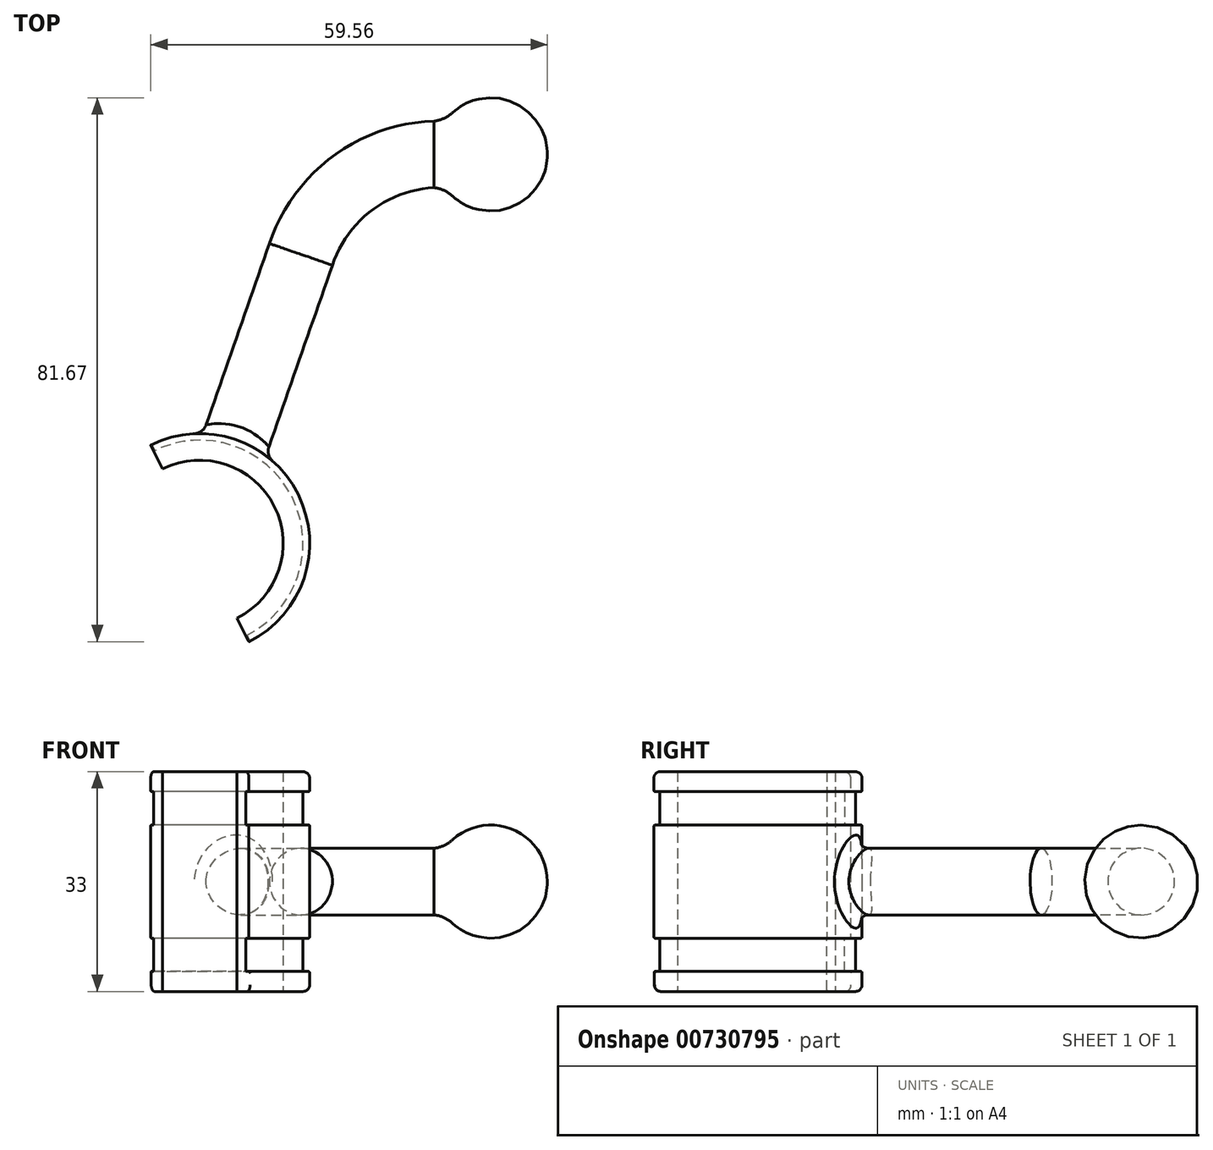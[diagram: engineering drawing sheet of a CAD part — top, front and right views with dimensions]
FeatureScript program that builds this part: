
annotation { "Feature Type Name" : "Feature", "Feature Type Description" : "" }
export const myFeature = defineFeature(function(context is Context, id is Id, definition is map)
    precondition{}
    {
        {
            var Q0;
            Q0=qCreatedBy(makeId("Top.planeOp"),FACE);
            var sketch = newSketch(context, id + "F0", { "sketchPlane" : qUnion([Q0])});
            skLineSegment(sketch, "E0", {"start": v(-8.5, 0) * mm, "end": v(-11.82, 0) * mm});
            skArc(sketch, "E1", {"start": v(8.5, 0) * mm, "mid": v(2.63, 8.08) * mm, "end": v(-6.87, 5) * mm});
            skLineSegment(sketch, "E2", {"start": v(50.87, 0) * mm, "end": v(0, 0) * mm, "construction": true});
            skLineSegment(sketch, "E3", {"start": v(8.5, 0) * mm, "end": v(0, 0) * mm});
            skLineSegment(sketch, "E4", {"start": v(-11.82, 0) * mm, "end": v(-5.91, 0) * mm});
            skLineSegment(sketch, "E5", {"start": v(-5.91, 0) * mm, "end": v(0, 0) * mm});
            skPoint(sketch, "E6", {"position": v(-28.5, -15) * mm});
            skLineSegment(sketch, "E7", {"start": v(0, 0) * mm, "end": v(-93.44, 0) * mm, "construction": true});
            skLineSegment(sketch, "E8", {"start": v(-8.5, 5) * mm, "end": v(-6.87, 5) * mm});
            skLineSegment(sketch, "E9", {"start": v(-52.11, -35.8) * mm, "end": v(-46.57, -38.1) * mm});
            skLineSegment(sketch, "E10", {"start": v(-8.5, 5) * mm, "end": v(-8.5, 0) * mm});
            skSolve(sketch);
        }
        {
            var Q0;
            Q0=makeQuery(id+"F0.imprint","IMPRINT",FACE,{"disambiguationData":[TD([[makeQuery(id+"F0.imprint","IMPRINT",EDGE,{"derivedFrom":sQuery(id+"F0.wireOp",EDGE,"E1")}),1.0]])]});
            var Q1;
            Q1=sQuery(id+"F0.wireOp",EDGE,"E3");
            revolve(context, id + "F1", {"surfaceOperationType" : NewSurfaceOperationType.NEW, "entities" : qUnion([Q0]), "axis" : qUnion([Q1]), "revolveType" : RevolveType.FULL});
        }
        {
            var Q0;
            Q0=makeQuery(id+"F1.opRevolve","SWEPT_FACE",FACE,{"disambiguationData":[OSD([sQuery(id+"F0.wireOp",EDGE,"E10")])]});
            var sketch = newSketch(context, id + "F2", { "sketchPlane" : qUnion([Q0])});
            skCircle(sketch, "E11.0", {"center": v(0, 0) * mm, "radius": 5 * mm});
            skSolve(sketch);
        }
        {
            var Q0;
            Q0=makeQuery(id+"F1.opRevolve","SWEPT_EDGE",EDGE,{"disambiguationData":[OSD([sQuery(id+"F0.wireOp",EDGE,"E1"),sQuery(id+"F0.wireOp",EDGE,"E8")])]});
            fillet(context, id + "F3", {"entities" : qUnion([Q0]), "radius" : 5 * mm, "tangentPropagation" : true, "allowEdgeOverflow" : false});
        }
        {
            var Q0;
            Q0=qCreatedBy(makeId("Top.planeOp"),FACE);
            var sketch = newSketch(context, id + "F4", { "sketchPlane" : qUnion([Q0])});
            skLineSegment(sketch, "E12.0", {"start": v(-33.35, -45.22) * mm, "end": v(-34.25, -44.88) * mm});
            skPoint(sketch, "E13.first.point", {"position": v(-38.02, -43.45) * mm});
            skPoint(sketch, "E13.second.point", {"position": v(-44.06, -59.28) * mm});
            skPoint(sketch, "E13.third.point", {"position": v(-42.18, -43.45) * mm});
            skPoint(sketch, "E13.third.point.positionSnap0", {"position": v(-38.02, -43.45) * mm});
            skPoint(sketch, "E14", {"position": v(-40.1, -51.73) * mm});
            skLineSegment(sketch, "E15", {"start": v(-38.02, -43.45) * mm, "end": v(-43.7, -58.41) * mm});
            skArc(sketch, "E16", {"start": v(-38.1, -69.6) * mm, "mid": v(-32.5, -52.83) * mm, "end": v(-49.27, -47.23) * mm});
            skLineSegment(sketch, "E17.0", {"start": v(-38.02, -43.45) * mm, "end": v(-38.02, -43.45) * mm});
            skArc(sketch, "E18.0", {"start": v(-36.32, -73.17) * mm, "mid": v(-28.93, -51.04) * mm, "end": v(-51.06, -43.65) * mm});
            skLineSegment(sketch, "E19", {"start": v(-51.06, -43.65) * mm, "end": v(-49.27, -47.23) * mm});
            skLineSegment(sketch, "E20", {"start": v(-38.1, -69.6) * mm, "end": v(-36.32, -73.17) * mm});
            skPoint(sketch, "E21.orphan", {"position": v(-42.7, -41.68) * mm});
            skPoint(sketch, "E22.trimOffspring.end.orphan", {"position": v(-41.8, -42.02) * mm});
            skSolve(sketch);
        }
        {
            var Q0;
            {var subQ0=sQuery(id+"F4.wireOp",EDGE,"E19");Q0=makeQuery(id+"F4.imprint","IMPRINT",FACE,{"disambiguationData":[TD([[makeQuery(id+"F4.imprint","IMPRINT",EDGE,{"derivedFrom":subQ0}),1.0]])]});}
            var Q1;
            {var subQ4=sQuery(id+"F4.wireOp",EDGE,"E13");Q1=makeQuery(id+"F4.imprint","IMPRINT",FACE,{"disambiguationData":[TD([[makeQuery(id+"F4.imprint","IMPRINT",EDGE,{"derivedFrom":subQ4}),1.0]])]});}
            extrude(context, id + "F5", {"entities" : qUnion([Q0, Q1]), "operationType" : NewBodyOperationType.ADD, "endBound" : BoundingType.SYMMETRIC, "depth" : 17 * mm, "offsetDistance" : 25 * mm});
        }
        {
            var Q0;
            Q0=makeQuery(id+"F5.opExtrude","CAP_FACE",FACE,{"disambiguationData":[OSD([sQuery(id+"F4.wireOp",EDGE,"E12.0"),sQuery(id+"F4.wireOp",EDGE,"E13"),sQuery(id+"F4.wireOp",EDGE,"E22.trimOffspring"),sQuery(id+"F4.wireOp",EDGE,"E16"),sQuery(id+"F4.wireOp",EDGE,"E18.0"),sQuery(id+"F4.wireOp",EDGE,"E19"),sQuery(id+"F4.wireOp",EDGE,"E20")])],"isStart":false});
            var sketch = newSketch(context, id + "F6", { "sketchPlane" : qUnion([Q0])});
            skArc(sketch, "E23.0", {"start": v(-38.1, -69.6) * mm, "mid": v(-32.5, -52.83) * mm, "end": v(-49.27, -47.23) * mm});
            skArc(sketch, "E24.0", {"start": v(-36.77, -72.28) * mm, "mid": v(-29.82, -51.49) * mm, "end": v(-50.61, -44.54) * mm});
            skLineSegment(sketch, "E25", {"start": v(-49.27, -47.23) * mm, "end": v(-50.61, -44.54) * mm});
            skLineSegment(sketch, "E26", {"start": v(-36.77, -72.28) * mm, "end": v(-38.1, -69.6) * mm});
            skSolve(sketch);
        }
        {
            var Q0;
            Q0=makeQuery(id+"F6.imprint","IMPRINT",FACE,{"disambiguationData":[TD([[makeQuery(id+"F6.imprint","IMPRINT",EDGE,{"derivedFrom":sQuery(id+"F6.wireOp",EDGE,"E23.0")}),-1.0]])]});
            extrude(context, id + "F7", {"entities" : qUnion([Q0]), "depth" : 5 * mm, "offsetDistance" : 25 * mm});
        }
        {
            var Q0;
            Q0=makeQuery(id+"F7.opExtrude","CAP_FACE",FACE,{"disambiguationData":[OSD([sQuery(id+"F6.wireOp",EDGE,"E23.0"),sQuery(id+"F6.wireOp",EDGE,"E24.0"),sQuery(id+"F6.wireOp",EDGE,"E25"),sQuery(id+"F6.wireOp",EDGE,"E26")])],"isStart":false});
            var sketch = newSketch(context, id + "F8", { "sketchPlane" : qUnion([Q0])});
            skArc(sketch, "E27.0", {"start": v(-36.32, -73.17) * mm, "mid": v(-28.93, -51.04) * mm, "end": v(-51.06, -43.65) * mm});
            skLineSegment(sketch, "E28.0", {"start": v(-36.32, -73.17) * mm, "end": v(-36.32, -73.17) * mm});
            skArc(sketch, "E29.0", {"start": v(-38.1, -69.6) * mm, "mid": v(-32.5, -52.83) * mm, "end": v(-49.27, -47.23) * mm});
            skLineSegment(sketch, "E30", {"start": v(-51.06, -43.65) * mm, "end": v(-49.27, -47.23) * mm});
            skLineSegment(sketch, "E31", {"start": v(-36.32, -73.17) * mm, "end": v(-38.1, -69.6) * mm});
            skSolve(sketch);
        }
        {
            var Q0;
            {var subQ0=sQuery(id+"F8.wireOp",EDGE,"E29.0");Q0=makeQuery(id+"F8.imprint","IMPRINT",FACE,{"disambiguationData":[TD([[makeQuery(id+"F8.imprint","IMPRINT",EDGE,{"derivedFrom":subQ0}),-1.0]])]});}
            var Q1;
            {var subQ5=makeQuery(id+"F7.opExtrude","CAP_EDGE",EDGE,{"disambiguationData":[OSD([sQuery(id+"F6.wireOp",EDGE,"E24.0")])],"isStart":false});Q1=makeQuery(id+"F8.imprint","IMPRINT",FACE,{"disambiguationData":[TD([[makeQuery(id+"F8.imprint","IMPRINT",EDGE,{"derivedFrom":subQ5}),-1.0]])]});}
            extrude(context, id + "F9", {"entities" : qUnion([Q0, Q1]), "operationType" : NewBodyOperationType.ADD, "depth" : 3 * mm, "offsetDistance" : 25 * mm});
        }
        {
            var Q0;
            Q0=makeQuery(id+"F7.opExtrude","SWEPT_BODY",BODY,{"disambiguationData":[OSD([sQuery(id+"F6.wireOp",EDGE,"E23.0"),sQuery(id+"F6.wireOp",EDGE,"E24.0"),sQuery(id+"F6.wireOp",EDGE,"E25"),sQuery(id+"F6.wireOp",EDGE,"E26")])]});
            var Q1;
            Q1=qCreatedBy(makeId("Top.planeOp"),FACE);
            mirror(context, id + "F10", {"operationType" : NewBodyOperationType.ADD, "entities" : qUnion([Q0]), "mirrorPlane" : qUnion([Q1])});
        }
        {
            var Q0;
            Q0=makeQuery(id+"F10.opPattern","COPY",EDGE,{"derivedFrom":makeQuery(id+"F9.opExtrude","CAP_EDGE",EDGE,{"disambiguationData":[OSD([sQuery(id+"F8.wireOp",EDGE,"E27.0")])],"isStart":false}),"instanceName":"1"});
            var Q1;
            Q1=makeQuery(id+"F9.opExtrude","CAP_EDGE",EDGE,{"disambiguationData":[OSD([sQuery(id+"F8.wireOp",EDGE,"E27.0")])],"isStart":false});
            fillet(context, id + "F11", {"entities" : qUnion([Q0, Q1]), "radius" : 1 * mm, "tangentPropagation" : true, "allowEdgeOverflow" : false});
        }
        {
            var Q0;
            {var subQ0=sQuery(id+"F4.wireOp",EDGE,"E18.0");Q0=makeQuery(id+"F5.opExtrude","CAP_EDGE",EDGE,{"disambiguationData":[OSD([subQ0]),TDD([makeQuery(id+"F4.imprint","IMPRINT",EDGE,{"disambiguationData":[TD([[makeQuery(id+"F4.imprint","INTERSECT",VERTEX,{"derivedFrom":[subQ0,sQuery(id+"F4.wireOp",EDGE,"E19")]}),1.0]])],"derivedFrom":subQ0})])],"isStart":false});}
            var Q1;
            Q1=makeQuery(id+"F9.opExtrude","CAP_EDGE",EDGE,{"disambiguationData":[OSD([sQuery(id+"F8.wireOp",EDGE,"E27.0")])],"isStart":true});
            var Q2;
            Q2=makeQuery(id+"F10.opPattern","COPY",FACE,{"derivedFrom":makeQuery(id+"F9.opExtrude","SWEPT_FACE",FACE,{"disambiguationData":[OSD([sQuery(id+"F8.wireOp",EDGE,"E27.0")])]}),"instanceName":"1"});
            var Q3;
            {var subQ0=sQuery(id+"F4.wireOp",EDGE,"E18.0");Q3=makeQuery(id+"F5.opExtrude","CAP_EDGE",EDGE,{"disambiguationData":[OSD([subQ0]),TDD([makeQuery(id+"F4.imprint","IMPRINT",EDGE,{"disambiguationData":[TD([[makeQuery(id+"F4.imprint","INTERSECT",VERTEX,{"derivedFrom":[subQ0,sQuery(id+"F4.wireOp",EDGE,"E19")]}),1.0]])],"derivedFrom":subQ0})])],"isStart":true});}
            var Q4;
            Q4=makeQuery(id+"F5.opExtrude","CAP_EDGE",EDGE,{"disambiguationData":[OSD([sQuery(id+"F4.wireOp",EDGE,"E22.trimOffspring")])],"isStart":true});
            var Q5;
            Q5=makeQuery(id+"F5.opExtrude","CAP_EDGE",EDGE,{"disambiguationData":[OSD([sQuery(id+"F4.wireOp",EDGE,"E13")])],"isStart":true});
            var Q6;
            Q6=makeQuery(id+"F5.opExtrude","CAP_EDGE",EDGE,{"disambiguationData":[OSD([sQuery(id+"F4.wireOp",EDGE,"E12.0")])],"isStart":true});
            var Q7;
            {var subQ0=sQuery(id+"F4.wireOp",EDGE,"E18.0");Q7=makeQuery(id+"F5.opExtrude","CAP_EDGE",EDGE,{"disambiguationData":[OSD([subQ0]),TDD([makeQuery(id+"F4.imprint","IMPRINT",EDGE,{"disambiguationData":[TD([[makeQuery(id+"F4.imprint","INTERSECT",VERTEX,{"derivedFrom":[subQ0,sQuery(id+"F4.wireOp",EDGE,"E20")]}),-1.0]])],"derivedFrom":subQ0})])],"isStart":true});}
            var Q8;
            Q8=makeQuery(id+"F5.opExtrude","CAP_EDGE",EDGE,{"disambiguationData":[OSD([sQuery(id+"F4.wireOp",EDGE,"E22.trimOffspring")])],"isStart":false});
            var Q9;
            Q9=makeQuery(id+"F5.opExtrude","CAP_EDGE",EDGE,{"disambiguationData":[OSD([sQuery(id+"F4.wireOp",EDGE,"E13")])],"isStart":false});
            var Q10;
            Q10=makeQuery(id+"F5.opExtrude","CAP_EDGE",EDGE,{"disambiguationData":[OSD([sQuery(id+"F4.wireOp",EDGE,"E12.0")])],"isStart":false});
            var Q11;
            {var subQ0=sQuery(id+"F4.wireOp",EDGE,"E18.0");Q11=makeQuery(id+"F5.opExtrude","CAP_EDGE",EDGE,{"disambiguationData":[OSD([subQ0]),TDD([makeQuery(id+"F4.imprint","IMPRINT",EDGE,{"disambiguationData":[TD([[makeQuery(id+"F4.imprint","INTERSECT",VERTEX,{"derivedFrom":[subQ0,sQuery(id+"F4.wireOp",EDGE,"E20")]}),-1.0]])],"derivedFrom":subQ0})])],"isStart":false});}
            var Q12;
            Q12=makeQuery(id+"F7.opExtrude","CAP_EDGE",EDGE,{"disambiguationData":[OSD([sQuery(id+"F6.wireOp",EDGE,"E24.0")])],"isStart":true});
            var Q13;
            Q13=makeQuery(id+"F7.opExtrude","CAP_EDGE",EDGE,{"disambiguationData":[OSD([sQuery(id+"F6.wireOp",EDGE,"E24.0")])],"isStart":false});
            var Q14;
            Q14=makeQuery(id+"F10.opPattern","COPY",EDGE,{"derivedFrom":makeQuery(id+"F7.opExtrude","CAP_EDGE",EDGE,{"disambiguationData":[OSD([sQuery(id+"F6.wireOp",EDGE,"E24.0")])],"isStart":true}),"instanceName":"1"});
            var Q15;
            Q15=makeQuery(id+"F10.opPattern","COPY",EDGE,{"derivedFrom":makeQuery(id+"F7.opExtrude","CAP_EDGE",EDGE,{"disambiguationData":[OSD([sQuery(id+"F6.wireOp",EDGE,"E24.0")])],"isStart":false}),"instanceName":"1"});
            fillet(context, id + "F12", {"entities" : qUnion([Q0, Q1, Q2, Q3, Q4, Q5, Q6, Q7, Q8, Q9, Q10, Q11, Q12, Q13, Q14, Q15]), "radius" : 0.2 * mm, "tangentPropagation" : true, "allowEdgeOverflow" : false});
        }
        {
            var Q0;
            Q0=qCreatedBy(makeId("Top.planeOp"),FACE);
            var sketch = newSketch(context, id + "F13", { "sketchPlane" : qUnion([Q0])});
            skLineSegment(sketch, "E32.0", {"start": v(-8.5, -5) * mm, "end": v(-8.5, 5) * mm});
            skArc(sketch, "E33", {"start": v(-8.5, 0) * mm, "mid": v(-20.84, -4.38) * mm, "end": v(-28.5, -15) * mm});
            skLineSegment(sketch, "E34", {"start": v(0, 0) * mm, "end": v(-39.55, 0) * mm, "construction": true});
            skArc(sketch, "E35.0", {"start": v(-51.06, -43.65) * mm, "mid": v(-28.93, -51.04) * mm, "end": v(-36.32, -73.17) * mm});
            skLineSegment(sketch, "E36", {"start": v(-38.24, -42.84) * mm, "end": v(-28.5, -15) * mm});
            skSolve(sketch);
        }
        {
            var Q0;
            Q0=makeQuery(id+"F2.imprint","IMPRINT",FACE,{"disambiguationData":[TD([[makeQuery(id+"F2.imprint","IMPRINT",EDGE,{"derivedFrom":sQuery(id+"F2.wireOp",EDGE,"E11.0")}),-1.0]])]});
            var Q1;
            Q1=sQuery(id+"F13.wireOp",EDGE,"E33");
            var Q2;
            Q2=sQuery(id+"F13.wireOp",EDGE,"E36");
            sweep(context, id + "F14", {"profiles" : qUnion([Q0]), "path" : qUnion([Q1, Q2])});
        }
        {
            var Q0;
            Q0=makeQuery(id+"F5.opExtrude","SWEPT_BODY",BODY,{"disambiguationData":[OSD([sQuery(id+"F4.wireOp",EDGE,"E16"),sQuery(id+"F4.wireOp",EDGE,"E18.0"),sQuery(id+"F4.wireOp",EDGE,"E19"),sQuery(id+"F4.wireOp",EDGE,"E20")])]});
            var Q1;
            Q1=makeQuery(id+"F14.opSweep","SWEPT_BODY",BODY,{"disambiguationData":[OSD([sQuery(id+"F2.wireOp",EDGE,"E11.0"),sQuery(id+"F13.wireOp",EDGE,"E36")])]});
            var Q2;
            Q2=makeQuery(id+"F1.opRevolve","SWEPT_BODY",BODY,{"disambiguationData":[OSD([sQuery(id+"F0.wireOp",EDGE,"E1"),sQuery(id+"F0.wireOp",EDGE,"E3"),sQuery(id+"F0.wireOp",EDGE,"E4"),sQuery(id+"F0.wireOp",EDGE,"E5"),sQuery(id+"F0.wireOp",EDGE,"E8"),sQuery(id+"F0.wireOp",EDGE,"E10")])]});
            booleanBodies(context, id + "F15", {"operationType" : BooleanOperationType.UNION, "tools" : qUnion([Q0, Q1, Q2])});
        }
        {
            var Q0;
            Q0=makeQuery(id+"F15.opBoolean","SPLIT",EDGE,{"disambiguationData":[OD(0.0)],"derivedFrom":makeQuery(id+"F14.opSweep","CAP_EDGE",EDGE,{"disambiguationData":[OSD([sQuery(id+"F2.wireOp",EDGE,"E11.0"),sQuery(id+"F13.wireOp",VERTEX,"E36.start")])],"isStart":false})});
            var Q1;
            Q1=makeQuery(id+"F15.opBoolean","SPLIT",EDGE,{"disambiguationData":[OD(1.0)],"derivedFrom":makeQuery(id+"F14.opSweep","CAP_EDGE",EDGE,{"disambiguationData":[OSD([sQuery(id+"F2.wireOp",EDGE,"E11.0"),sQuery(id+"F13.wireOp",VERTEX,"E36.start")])],"isStart":false})});
            var Q2;
            Q2=makeQuery(id+"F15.opBoolean","INTERSECT",EDGE,{"disambiguationData":[OD(1.0)],"derivedFrom":[makeQuery(id+"F5.opExtrude","SWEPT_FACE",FACE,{"disambiguationData":[OSD([sQuery(id+"F4.wireOp",EDGE,"E18.0")])]}),makeQuery(id+"F14.opSweep","SWEPT_FACE",FACE,{"disambiguationData":[OSD([sQuery(id+"F2.wireOp",EDGE,"E11.0"),sQuery(id+"F13.wireOp",EDGE,"E36")])]})]});
            var Q3;
            Q3=makeQuery(id+"F15.opBoolean","INTERSECT",EDGE,{"disambiguationData":[OD(0.0)],"derivedFrom":[makeQuery(id+"F5.opExtrude","SWEPT_FACE",FACE,{"disambiguationData":[OSD([sQuery(id+"F4.wireOp",EDGE,"E18.0")])]}),makeQuery(id+"F14.opSweep","SWEPT_FACE",FACE,{"disambiguationData":[OSD([sQuery(id+"F2.wireOp",EDGE,"E11.0"),sQuery(id+"F13.wireOp",EDGE,"E36")])]})]});
            fillet(context, id + "F16", {"entities" : qUnion([Q0, Q1, Q2, Q3]), "radius" : 2 * mm, "tangentPropagation" : true, "allowEdgeOverflow" : false});
        }
    });
